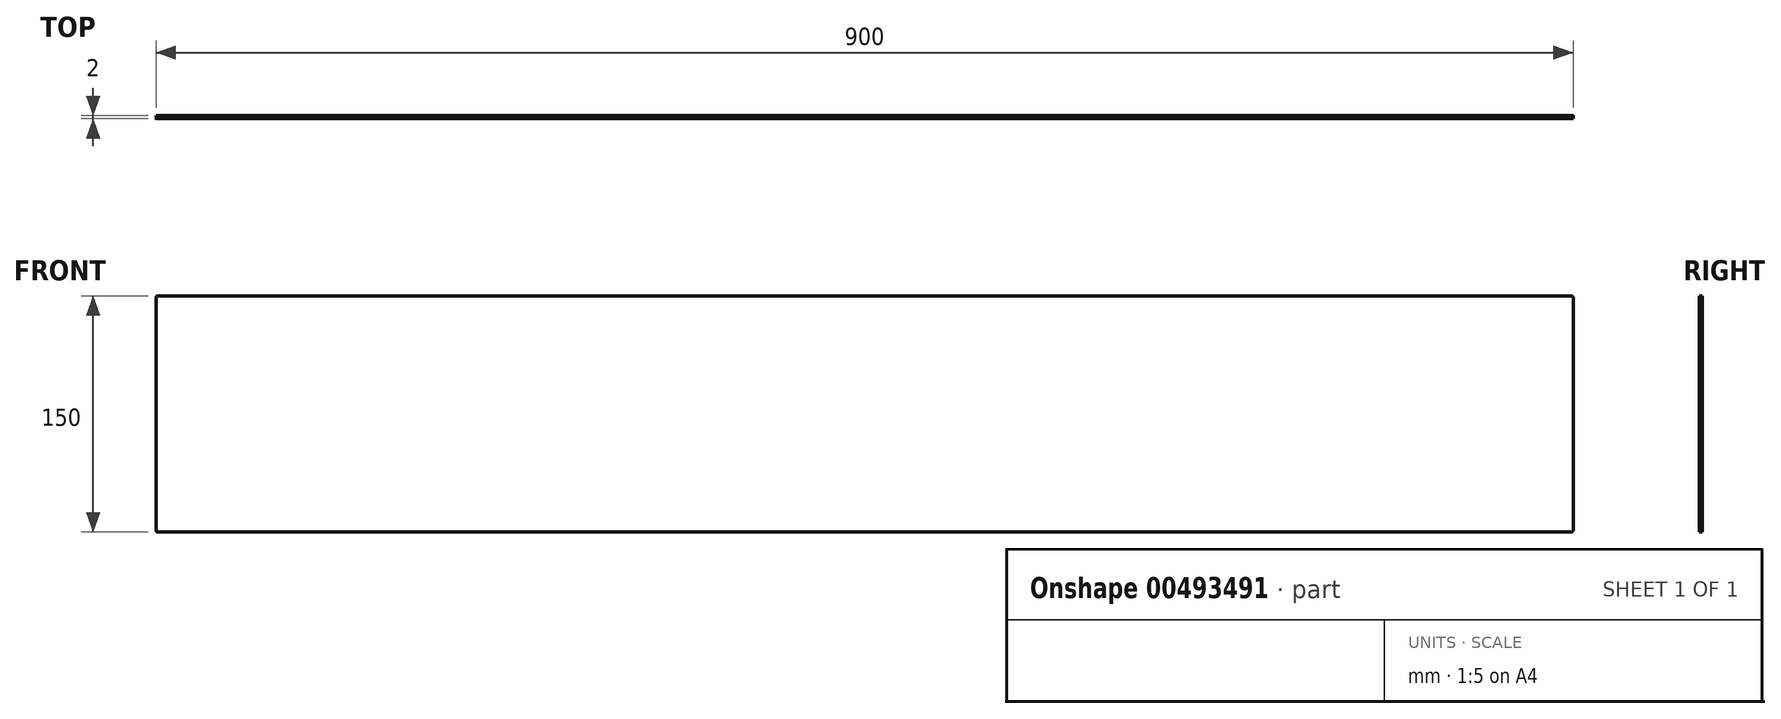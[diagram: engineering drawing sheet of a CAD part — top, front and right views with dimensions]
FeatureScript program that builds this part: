
annotation { "Feature Type Name" : "Feature", "Feature Type Description" : "" }
export const myFeature = defineFeature(function(context is Context, id is Id, definition is map)
    precondition{}
    {
        {
            var Q0;
            Q0=qCreatedBy(makeId("Front.planeOp"),FACE);
            var sketch = newSketch(context, id + "F0", { "sketchPlane" : qUnion([Q0])});
            skLineSegment(sketch, "E0.bottom", {"start": v(-450, 75) * mm, "end": v(450, 75) * mm});
            skLineSegment(sketch, "E0.top", {"start": v(-450, -75) * mm, "end": v(450, -75) * mm});
            skLineSegment(sketch, "E0.left", {"start": v(-450, 75) * mm, "end": v(-450, -75) * mm});
            skLineSegment(sketch, "E0.right", {"start": v(450, 75) * mm, "end": v(450, -75) * mm});
            skPoint(sketch, "E1.oppositeSnap0", {"position": v(0, 75) * mm});
            skLineSegment(sketch, "E2", {"start": v(-72.97, 0) * mm, "end": v(73.63, 0) * mm, "construction": true});
            skLineSegment(sketch, "E3", {"start": v(0, 70.28) * mm, "end": v(0, -60.49) * mm, "construction": true});
            skSolve(sketch);
        }
        {
            var Q0;
            Q0=qSketchRegion(id+"F0",true);
            extrude(context, id + "F1", {"entities" : qUnion([Q0]), "depth" : 2 * mm});
        }
        {
            var Q0;
            Q0=makeQuery(id+"F1.opExtrude","SWEPT_EDGE",EDGE,{"disambiguationData":[OSD([sQuery(id+"F0.wireOp",EDGE,"E0.bottom"),sQuery(id+"F0.wireOp",EDGE,"E0.right")])]});
            var Q1;
            Q1=makeQuery(id+"F1.opExtrude","SWEPT_EDGE",EDGE,{"disambiguationData":[OSD([sQuery(id+"F0.wireOp",EDGE,"E0.top"),sQuery(id+"F0.wireOp",EDGE,"E0.right")])]});
            var Q2;
            Q2=makeQuery(id+"F1.opExtrude","SWEPT_EDGE",EDGE,{"disambiguationData":[OSD([sQuery(id+"F0.wireOp",EDGE,"E0.top"),sQuery(id+"F0.wireOp",EDGE,"E0.left")])]});
            var Q3;
            Q3=makeQuery(id+"F1.opExtrude","SWEPT_EDGE",EDGE,{"disambiguationData":[OSD([sQuery(id+"F0.wireOp",EDGE,"E0.bottom"),sQuery(id+"F0.wireOp",EDGE,"E0.left")])]});
            fillet(context, id + "F2", {"entities" : qUnion([Q0, Q1, Q2, Q3]), "radius" : 1 * mm, "tangentPropagation" : true, "allowEdgeOverflow" : false});
        }
    });
